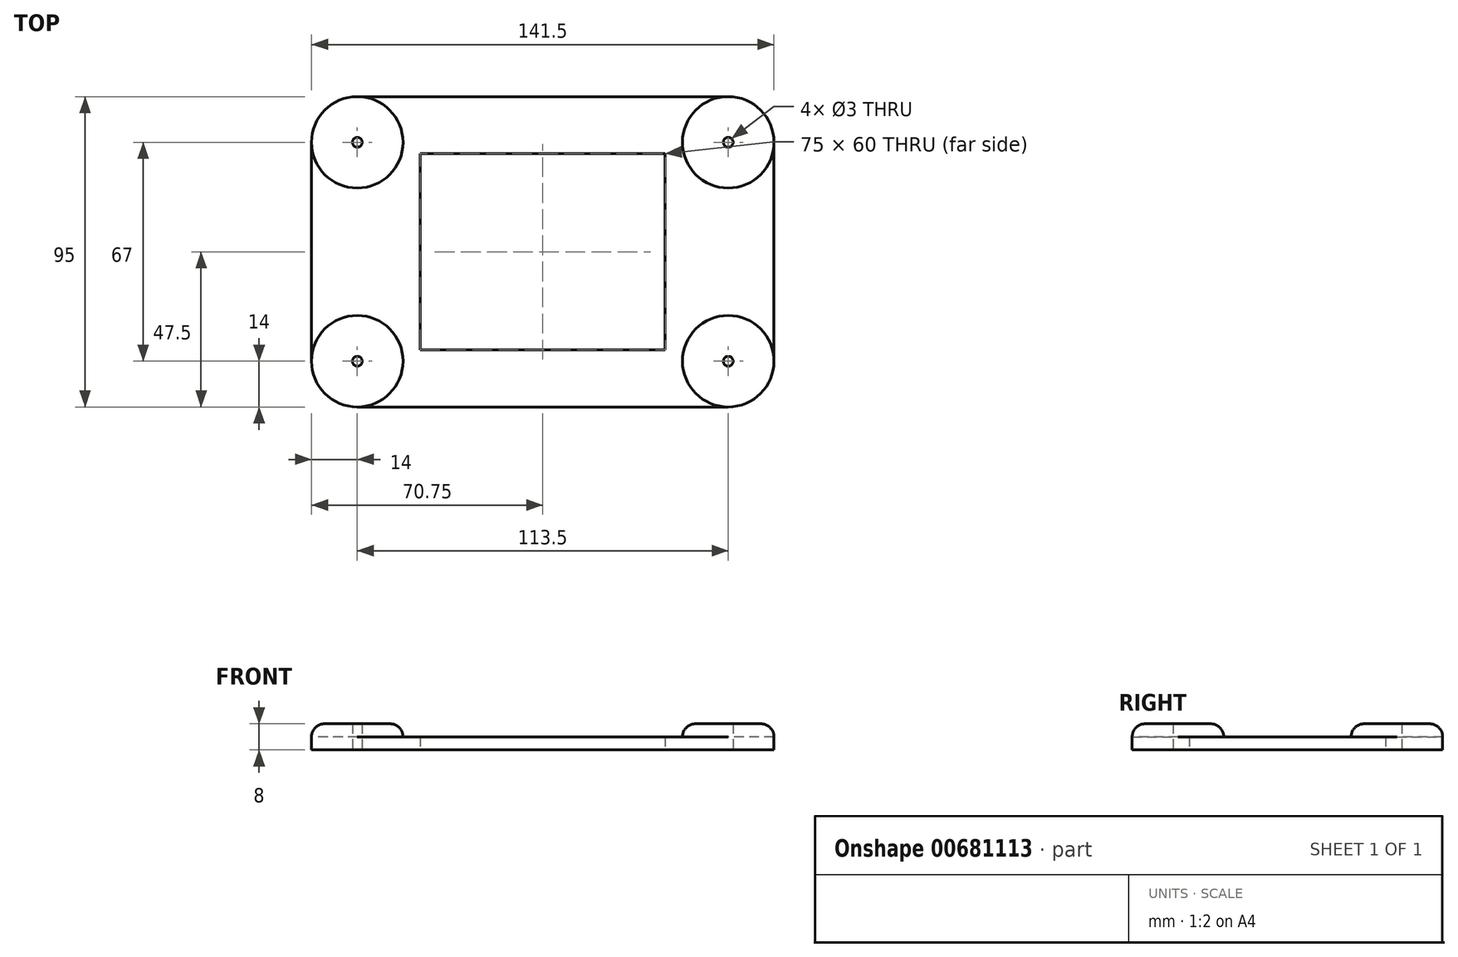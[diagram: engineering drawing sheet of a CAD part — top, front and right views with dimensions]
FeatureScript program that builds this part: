
annotation { "Feature Type Name" : "Feature", "Feature Type Description" : "" }
export const myFeature = defineFeature(function(context is Context, id is Id, definition is map)
    precondition{}
    {
        {
            var Q0;
            Q0=qCreatedBy(makeId("Top.planeOp"),FACE);
            var sketch = newSketch(context, id + "F0", { "sketchPlane" : qUnion([Q0])});
            skLineSegment(sketch, "E0.bottom", {"start": v(-70.75, 47.5) * mm, "end": v(70.75, 47.5) * mm});
            skLineSegment(sketch, "E0.top", {"start": v(-70.75, -47.5) * mm, "end": v(70.75, -47.5) * mm});
            skLineSegment(sketch, "E0.left", {"start": v(-70.75, 47.5) * mm, "end": v(-70.75, -47.5) * mm});
            skLineSegment(sketch, "E0.right", {"start": v(70.75, 47.5) * mm, "end": v(70.75, -47.5) * mm});
            skPoint(sketch, "E0.middle", {"position": v(0, 0) * mm});
            skLineSegment(sketch, "E1.bottom", {"start": v(-56.75, 33.5) * mm, "end": v(56.75, 33.5) * mm, "construction": true});
            skLineSegment(sketch, "E1.top", {"start": v(-56.75, -33.5) * mm, "end": v(56.75, -33.5) * mm, "construction": true});
            skLineSegment(sketch, "E1.left", {"start": v(-56.75, 33.5) * mm, "end": v(-56.75, -33.5) * mm, "construction": true});
            skLineSegment(sketch, "E1.right", {"start": v(56.75, 33.5) * mm, "end": v(56.75, -33.5) * mm, "construction": true});
            skCircle(sketch, "E2", {"center": v(-56.75, 33.5) * mm, "radius": 1.5 * mm});
            skCircle(sketch, "E3", {"center": v(-56.75, -33.5) * mm, "radius": 1.5 * mm});
            skCircle(sketch, "E4", {"center": v(56.75, -33.5) * mm, "radius": 1.5 * mm});
            skCircle(sketch, "E5", {"center": v(56.75, 33.5) * mm, "radius": 1.5 * mm});
            skLineSegment(sketch, "E6.bottom", {"start": v(37.5, -30) * mm, "end": v(-37.5, -30) * mm});
            skLineSegment(sketch, "E6.top", {"start": v(37.5, 30) * mm, "end": v(-37.5, 30) * mm});
            skLineSegment(sketch, "E6.left", {"start": v(37.5, -30) * mm, "end": v(37.5, 30) * mm});
            skLineSegment(sketch, "E6.right", {"start": v(-37.5, -30) * mm, "end": v(-37.5, 30) * mm});
            skCircle(sketch, "E7", {"center": v(-56.75, 33.5) * mm, "radius": 14 * mm});
            skCircle(sketch, "E8", {"center": v(-56.75, -33.5) * mm, "radius": 14 * mm});
            skCircle(sketch, "E9", {"center": v(56.75, -33.5) * mm, "radius": 14 * mm});
            skCircle(sketch, "E10", {"center": v(56.75, 33.5) * mm, "radius": 14 * mm});
            skSolve(sketch);
        }
        {
            var Q0;
            Q0=makeQuery(id+"F0.imprint","IMPRINT",FACE,{"disambiguationData":[TD([[makeQuery(id+"F0.imprint","IMPRINT",EDGE,{"derivedFrom":sQuery(id+"F0.wireOp",EDGE,"E6.bottom")}),1.0]])]});
            extrude(context, id + "F1", {"entities" : qUnion([Q0]), "depth" : 4 * mm, "offsetDistance" : 25 * mm});
        }
        {
            var Q0;
            Q0=makeQuery(id+"F0.imprint","IMPRINT",FACE,{"disambiguationData":[TD([[makeQuery(id+"F0.imprint","IMPRINT",EDGE,{"derivedFrom":sQuery(id+"F0.wireOp",EDGE,"E2")}),-1.0]])]});
            var Q1;
            Q1=makeQuery(id+"F0.imprint","IMPRINT",FACE,{"disambiguationData":[TD([[makeQuery(id+"F0.imprint","IMPRINT",EDGE,{"derivedFrom":sQuery(id+"F0.wireOp",EDGE,"E3")}),-1.0]])]});
            var Q2;
            Q2=makeQuery(id+"F0.imprint","IMPRINT",FACE,{"disambiguationData":[TD([[makeQuery(id+"F0.imprint","IMPRINT",EDGE,{"derivedFrom":sQuery(id+"F0.wireOp",EDGE,"E4")}),-1.0]])]});
            var Q3;
            Q3=makeQuery(id+"F0.imprint","IMPRINT",FACE,{"disambiguationData":[TD([[makeQuery(id+"F0.imprint","IMPRINT",EDGE,{"derivedFrom":sQuery(id+"F0.wireOp",EDGE,"E5")}),-1.0]])]});
            extrude(context, id + "F2", {"entities" : qUnion([Q0, Q1, Q2, Q3]), "operationType" : NewBodyOperationType.ADD, "depth" : 8 * mm, "offsetDistance" : 25 * mm});
        }
        {
            var Q0;
            Q0=makeQuery(id+"F2.opExtrude","CAP_EDGE",EDGE,{"disambiguationData":[OSD([sQuery(id+"F0.wireOp",EDGE,"E7")])],"isStart":false});
            var Q1;
            Q1=makeQuery(id+"F2.opExtrude","CAP_EDGE",EDGE,{"disambiguationData":[OSD([sQuery(id+"F0.wireOp",EDGE,"E8")])],"isStart":false});
            var Q2;
            Q2=makeQuery(id+"F2.opExtrude","CAP_EDGE",EDGE,{"disambiguationData":[OSD([sQuery(id+"F0.wireOp",EDGE,"E9")])],"isStart":false});
            var Q3;
            Q3=makeQuery(id+"F2.opExtrude","CAP_EDGE",EDGE,{"disambiguationData":[OSD([sQuery(id+"F0.wireOp",EDGE,"E10")])],"isStart":false});
            fillet(context, id + "F3", {"entities" : qUnion([Q0, Q1, Q2, Q3]), "radius" : 4 * mm, "allowEdgeOverflow" : false});
        }
    });
